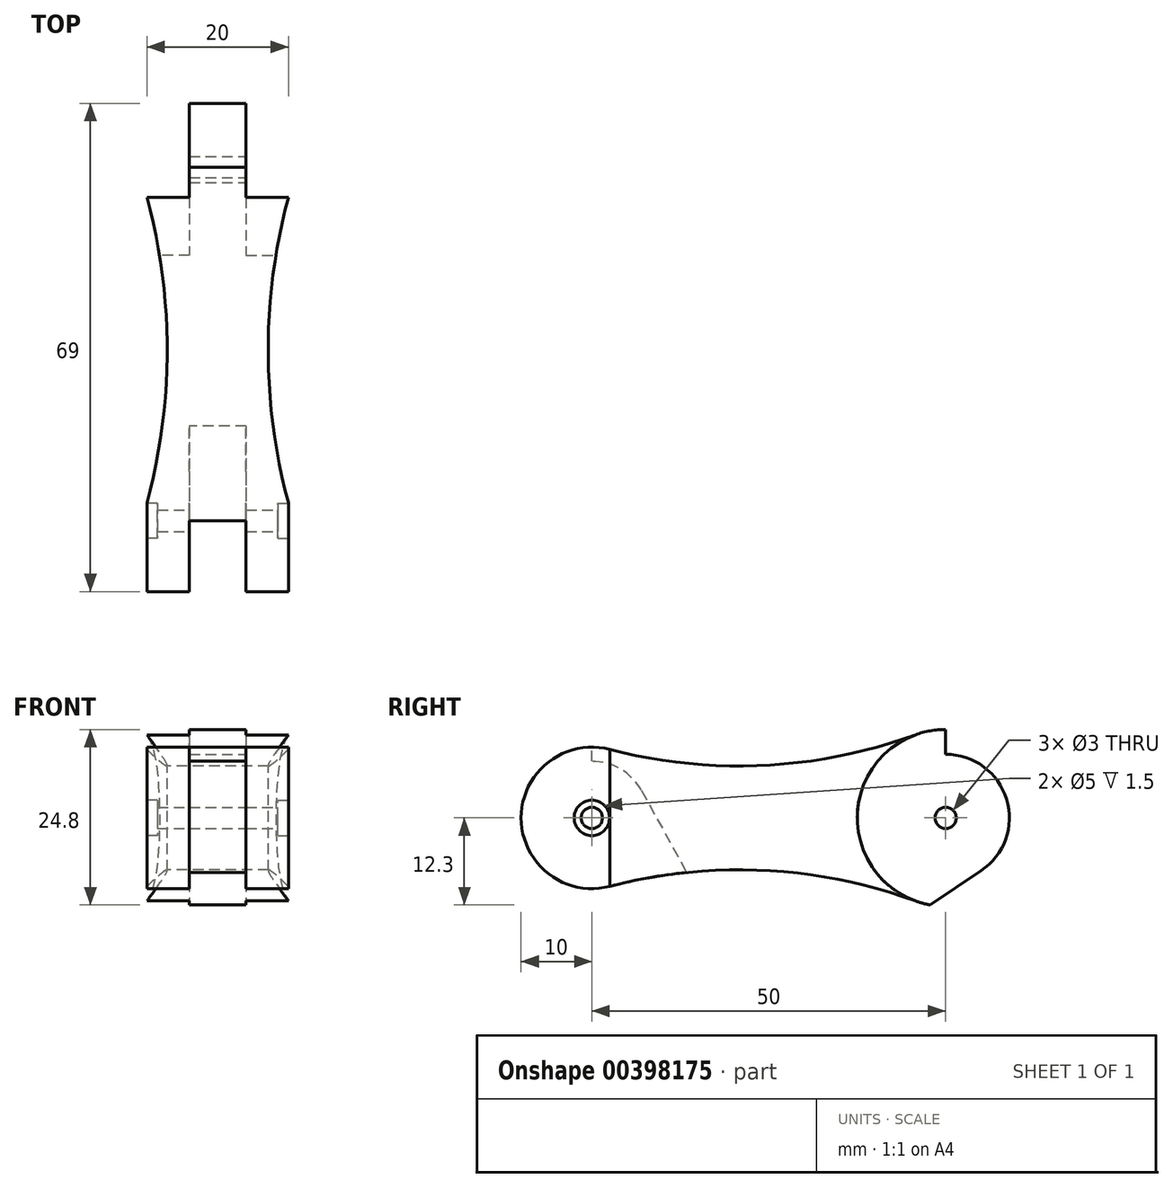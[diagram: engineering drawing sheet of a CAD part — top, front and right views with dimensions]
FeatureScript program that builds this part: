
annotation { "Feature Type Name" : "Feature", "Feature Type Description" : "" }
export const myFeature = defineFeature(function(context is Context, id is Id, definition is map)
    precondition{}
    {
        {
            var Q0;
            Q0=qCreatedBy(makeId("Right.planeOp"),FACE);
            var sketch = newSketch(context, id + "F0", { "sketchPlane" : qUnion([Q0])});
            skArc(sketch, "E0", {"start": v(2.52, 9.68) * mm, "mid": v(-10, 0) * mm, "end": v(2.52, -9.68) * mm});
            skLineSegment(sketch, "E1", {"start": v(-29.92, 0) * mm, "end": v(87.26, 0) * mm, "construction": true});
            skArc(sketch, "E2", {"start": v(45.71, -11.74) * mm, "mid": v(62.5, 0) * mm, "end": v(45.71, 11.74) * mm});
            skArc(sketch, "E3", {"start": v(2.52, 9.68) * mm, "mid": v(24.27, 7.42) * mm, "end": v(45.71, 11.74) * mm});
            skArc(sketch, "E4", {"start": v(45.71, -11.74) * mm, "mid": v(24.27, -7.42) * mm, "end": v(2.52, -9.68) * mm});
            skSolve(sketch);
        }
        {
            var Q0;
            Q0 = qSketchRegion(id + "F0", true);
            extrude(context, id + "F1", {"entities" : qUnion([Q0]), "depth" : 6 * mm});
        }
        {
            var Q0;
            Q0=makeQuery(id+"F1.opExtrude","CAP_FACE",FACE,{"disambiguationData":[OSD([sQuery(id+"F0.wireOp",EDGE,"E0"),sQuery(id+"F0.wireOp",EDGE,"E2"),sQuery(id+"F0.wireOp",EDGE,"E3"),sQuery(id+"F0.wireOp",EDGE,"E4")])],"isStart":false});
            var sketch = newSketch(context, id + "F2", { "sketchPlane" : qUnion([Q0])});
            skArc(sketch, "E5.0", {"start": v(2.52, 9.68) * mm, "mid": v(24.27, 7.42) * mm, "end": v(45.71, 11.74) * mm});
            skArc(sketch, "E6.0", {"start": v(2.52, 9.68) * mm, "mid": v(1.27, 9.92) * mm, "end": v(0, 10) * mm});
            skArc(sketch, "E7.0", {"start": v(45.71, -11.74) * mm, "mid": v(28.65, -7.76) * mm, "end": v(11.13, -7.99) * mm});
            skArc(sketch, "E8.0", {"start": v(45.71, -11.74) * mm, "mid": v(62.5, 0) * mm, "end": v(45.71, 11.74) * mm});
            skArc(sketch, "E9", {"start": v(8, 0) * mm, "mid": v(5.66, 5.66) * mm, "end": v(0, 8) * mm});
            skLineSegment(sketch, "E10", {"start": v(0, 8) * mm, "end": v(0, 10) * mm});
            skLineSegment(sketch, "E11", {"start": v(0, 0) * mm, "end": v(34.92, 0) * mm, "construction": true});
            skLineSegment(sketch, "E12", {"start": v(7, 3.87) * mm, "end": v(13.41, -7.72) * mm});
            skPoint(sketch, "E13.orphan", {"position": v(7, -3.87) * mm});
            skSolve(sketch);
        }
        {
            var Q0;
            Q0 = qSketchRegion(id + "F2", true);
            extrude(context, id + "F3", {"entities" : qUnion([Q0]), "operationType" : NewBodyOperationType.ADD, "depth" : 8 * mm});
        }
        {
            var Q0;
            Q0=makeQuery(id+"F3.opExtrude","CAP_FACE",FACE,{"disambiguationData":[OSD([sQuery(id+"F2.wireOp",EDGE,"E5.0"),sQuery(id+"F2.wireOp",EDGE,"E6.0"),sQuery(id+"F2.wireOp",EDGE,"E7.0"),sQuery(id+"F2.wireOp",EDGE,"E8.0"),sQuery(id+"F2.wireOp",EDGE,"E9"),sQuery(id+"F2.wireOp",EDGE,"E10"),sQuery(id+"F2.wireOp",EDGE,"JRJ70NO1-7vJe-Li3z-EIXT-plhISmGAnEbH")])],"isStart":false});
            var sketch = newSketch(context, id + "F4", { "sketchPlane" : qUnion([Q0])});
            skArc(sketch, "E14.0", {"start": v(0, 10) * mm, "mid": v(-9.92, -1.27) * mm, "end": v(2.52, -9.68) * mm});
            skArc(sketch, "E15.0", {"start": v(2.52, 9.68) * mm, "mid": v(24.27, 7.42) * mm, "end": v(45.71, 11.74) * mm});
            skArc(sketch, "E16.0", {"start": v(13.41, -7.72) * mm, "mid": v(7.93, -8.49) * mm, "end": v(2.52, -9.68) * mm});
            skLineSegment(sketch, "E17.0", {"start": v(45.71, -11.74) * mm, "end": v(45.71, -11.74) * mm});
            skArc(sketch, "E18.0", {"start": v(45.71, -11.74) * mm, "mid": v(62.5, 0) * mm, "end": v(45.71, 11.74) * mm});
            skArc(sketch, "E19.0", {"start": v(2.52, 9.68) * mm, "mid": v(1.27, 9.92) * mm, "end": v(0, 10) * mm});
            skArc(sketch, "E20.0", {"start": v(45.71, -11.74) * mm, "mid": v(29.8, -7.9) * mm, "end": v(13.41, -7.72) * mm});
            skSolve(sketch);
        }
        {
            var Q0;
            Q0 = qSketchRegion(id + "F4", true);
            extrude(context, id + "F5", {"entities" : qUnion([Q0]), "operationType" : NewBodyOperationType.ADD, "depth" : 6 * mm});
        }
        {
            var Q0;
            Q0=makeQuery(id+"F5.opExtrude","CAP_FACE",FACE,{"disambiguationData":[OSD([sQuery(id+"F4.wireOp",EDGE,"E14.0"),sQuery(id+"F4.wireOp",EDGE,"E15.0"),sQuery(id+"F4.wireOp",EDGE,"E16.0"),sQuery(id+"F4.wireOp",EDGE,"E17.0"),sQuery(id+"F4.wireOp",EDGE,"E18.0"),sQuery(id+"F4.wireOp",EDGE,"E19.0")])],"isStart":false});
            var sketch = newSketch(context, id + "F6", { "sketchPlane" : qUnion([Q0])});
            skCircle(sketch, "E21", {"center": v(50, 0) * mm, "radius": 12.5 * mm});
            skSolve(sketch);
        }
        {
            var Q0;
            Q0 = qSketchRegion(id + "F6", true);
            extrude(context, id + "F7", {"entities" : qUnion([Q0]), "operationType" : NewBodyOperationType.REMOVE, "oppositeDirection" : true, "depth" : 6 * mm});
        }
        {
            var Q0;
            Q0=makeQuery(id+"F1.opExtrude","CAP_FACE",FACE,{"disambiguationData":[OSD([sQuery(id+"F0.wireOp",EDGE,"E0"),sQuery(id+"F0.wireOp",EDGE,"E2"),sQuery(id+"F0.wireOp",EDGE,"E3"),sQuery(id+"F0.wireOp",EDGE,"E4")])],"isStart":true});
            var sketch = newSketch(context, id + "F8", { "sketchPlane" : qUnion([Q0])});
            skCircle(sketch, "E22", {"center": v(-50, 0) * mm, "radius": 12.5 * mm});
            skSolve(sketch);
        }
        {
            var Q0;
            Q0 = qSketchRegion(id + "F8", true);
            extrude(context, id + "F9", {"entities" : qUnion([Q0]), "operationType" : NewBodyOperationType.REMOVE, "oppositeDirection" : true, "depth" : 6 * mm});
        }
        {
            var Q0;
            Q0=makeQuery(id+"F7.boolean.opBoolean","COPY",FACE,{"derivedFrom":makeQuery(id+"F7.opExtrude","CAP_FACE",FACE,{"disambiguationData":[OSD([sQuery(id+"F6.wireOp",EDGE,"E21")])],"isStart":false})});
            var sketch = newSketch(context, id + "F10", { "sketchPlane" : qUnion([Q0])});
            skArc(sketch, "E23", {"start": v(47.79, -12.3) * mm, "mid": v(62.45, -1.11) * mm, "end": v(50, 12.5) * mm});
            skArc(sketch, "E24", {"start": v(55, -7.48) * mm, "mid": v(58.61, 2.61) * mm, "end": v(50, 9) * mm});
            skLineSegment(sketch, "E25", {"start": v(50, 12.5) * mm, "end": v(50, 9) * mm});
            skLineSegment(sketch, "E26", {"start": v(55, -7.48) * mm, "end": v(47.79, -12.3) * mm});
            skSolve(sketch);
        }
        {
            var Q0;
            Q0 = qSketchRegion(id + "F10", true);
            extrude(context, id + "F11", {"entities" : qUnion([Q0]), "operationType" : NewBodyOperationType.REMOVE, "endBound" : BoundingType.THROUGH_ALL, "oppositeDirection" : true, "depth" : 25 * mm});
        }
        {
            var Q0;
            Q0=makeQuery(id+"F5.opExtrude","CAP_FACE",FACE,{"disambiguationData":[OSD([sQuery(id+"F4.wireOp",EDGE,"E14.0"),sQuery(id+"F4.wireOp",EDGE,"E15.0"),sQuery(id+"F4.wireOp",EDGE,"E16.0"),sQuery(id+"F4.wireOp",EDGE,"E18.0"),sQuery(id+"F4.wireOp",EDGE,"E19.0"),sQuery(id+"F4.wireOp",EDGE,"E20.0")])],"isStart":false});
            var sketch = newSketch(context, id + "F12", { "sketchPlane" : qUnion([Q0])});
            skCircle(sketch, "E27", {"center": v(0, 0) * mm, "radius": 1.5 * mm});
            skCircle(sketch, "E28", {"center": v(50, 0) * mm, "radius": 1.5 * mm});
            skSolve(sketch);
        }
        {
            var Q0;
            Q0 = qSketchRegion(id + "F12", true);
            extrude(context, id + "F13", {"entities" : qUnion([Q0]), "operationType" : NewBodyOperationType.REMOVE, "endBound" : BoundingType.THROUGH_ALL, "oppositeDirection" : true, "depth" : 25 * mm});
        }
        {
            var Q0;
            Q0=makeQuery(id+"F5.opExtrude","CAP_FACE",FACE,{"disambiguationData":[OSD([sQuery(id+"F4.wireOp",EDGE,"E14.0"),sQuery(id+"F4.wireOp",EDGE,"E15.0"),sQuery(id+"F4.wireOp",EDGE,"E16.0"),sQuery(id+"F4.wireOp",EDGE,"E18.0"),sQuery(id+"F4.wireOp",EDGE,"E19.0"),sQuery(id+"F4.wireOp",EDGE,"E20.0")])],"isStart":false});
            var sketch = newSketch(context, id + "F14", { "sketchPlane" : qUnion([Q0])});
            skCircle(sketch, "E29", {"center": v(0, 0) * mm, "radius": 2.5 * mm});
            skSolve(sketch);
        }
        {
            var Q0;
            Q0 = qSketchRegion(id + "F14", true);
            extrude(context, id + "F15", {"entities" : qUnion([Q0]), "operationType" : NewBodyOperationType.REMOVE, "oppositeDirection" : true, "depth" : 1.5 * mm});
        }
        {
            var Q0;
            Q0=makeQuery(id+"F1.opExtrude","CAP_FACE",FACE,{"disambiguationData":[OSD([sQuery(id+"F0.wireOp",EDGE,"E0"),sQuery(id+"F0.wireOp",EDGE,"E2"),sQuery(id+"F0.wireOp",EDGE,"E3"),sQuery(id+"F0.wireOp",EDGE,"E4")])],"isStart":true});
            var sketch = newSketch(context, id + "F16", { "sketchPlane" : qUnion([Q0])});
            skCircle(sketch, "E30", {"center": v(0, 0) * mm, "radius": 2.5 * mm});
            skSolve(sketch);
        }
        {
            var Q0;
            Q0 = qSketchRegion(id + "F16", true);
            extrude(context, id + "F17", {"entities" : qUnion([Q0]), "operationType" : NewBodyOperationType.REMOVE, "oppositeDirection" : true, "depth" : 1.5 * mm});
        }
        {
            var Q0;
            Q0=qCreatedBy(makeId("Top.planeOp"),FACE);
            var sketch = newSketch(context, id + "F18", { "sketchPlane" : qUnion([Q0])});
            skCircle(sketch, "E31", {"center": v(-80, 24.12) * mm, "radius": 82.86 * mm});
            skCircle(sketch, "E32", {"center": v(100, 24.12) * mm, "radius": 82.86 * mm});
            skSolve(sketch);
        }
        {
            var Q0;
            Q0 = qSketchRegion(id + "F18", true);
            extrude(context, id + "F19", {"entities" : qUnion([Q0]), "operationType" : NewBodyOperationType.REMOVE, "endBound" : BoundingType.SYMMETRIC, "oppositeDirection" : true, "depth" : 25 * mm});
        }
    });
